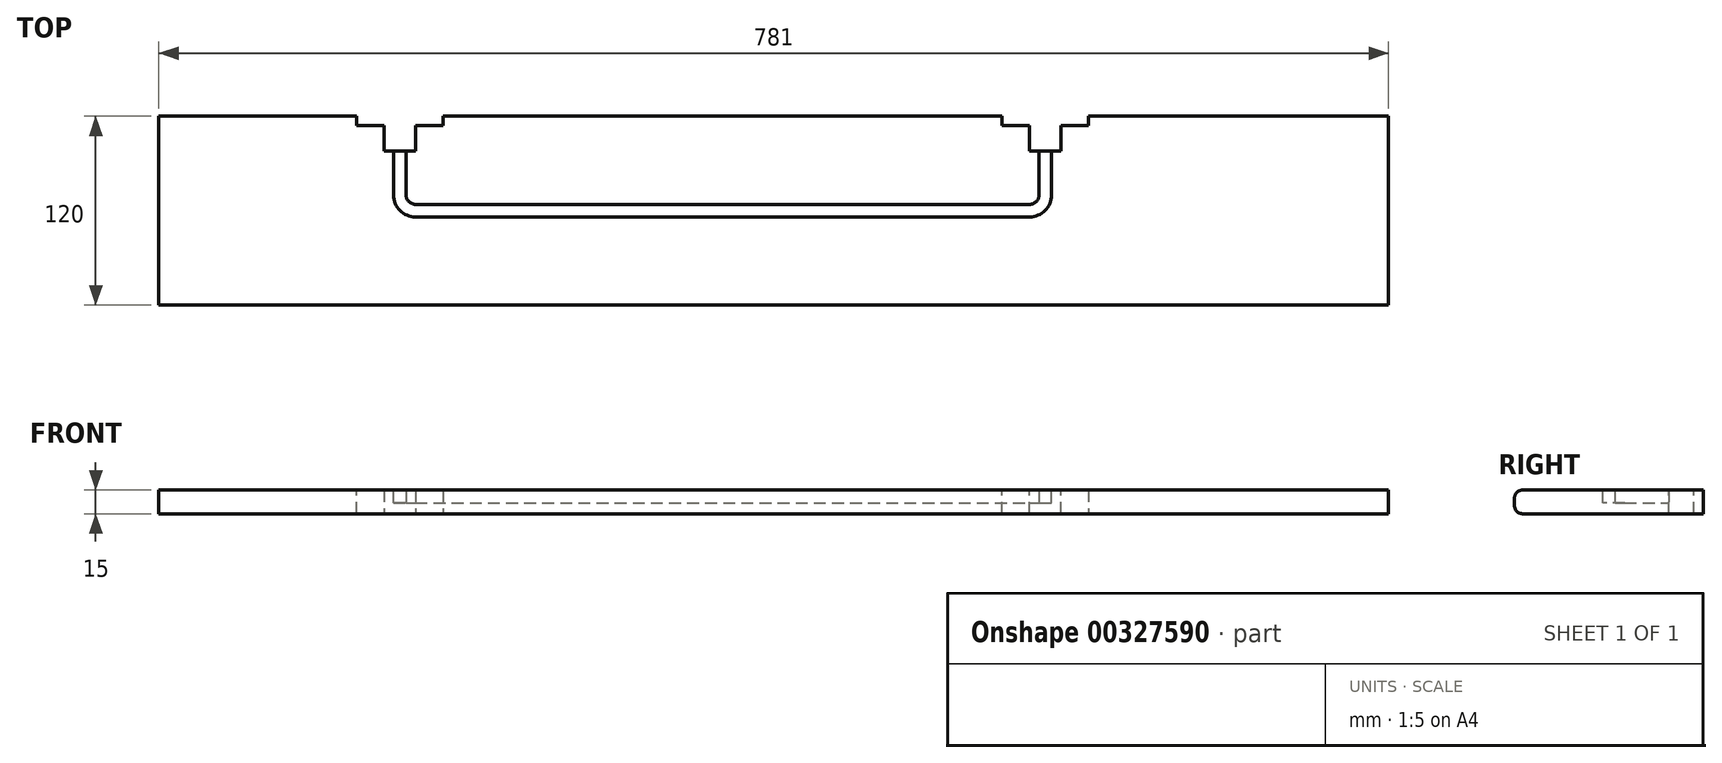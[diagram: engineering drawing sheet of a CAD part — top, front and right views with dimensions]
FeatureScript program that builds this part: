
annotation { "Feature Type Name" : "Feature", "Feature Type Description" : "" }
export const myFeature = defineFeature(function(context is Context, id is Id, definition is map)
    precondition{}
    {
        {
            var Q0;
            Q0=qCreatedBy(makeId("Right.planeOp"),FACE);
            var sketch = newSketch(context, id + "F0", { "sketchPlane" : qUnion([Q0])});
            skLineSegment(sketch, "E0.bottom", {"start": v(60, 7.5) * mm, "end": v(-60, 7.5) * mm});
            skLineSegment(sketch, "E0.top", {"start": v(60, -7.5) * mm, "end": v(-60, -7.5) * mm});
            skLineSegment(sketch, "E0.left", {"start": v(60, 7.5) * mm, "end": v(60, -7.5) * mm});
            skLineSegment(sketch, "E0.right", {"start": v(-60, 7.5) * mm, "end": v(-60, -7.5) * mm});
            skPoint(sketch, "E0.middle", {"position": v(0, 0) * mm});
            skSolve(sketch);
        }
        {
            var Q0;
            Q0=makeQuery(id+"F0.imprint","IMPRINT",FACE,{"disambiguationData":[TD([[makeQuery(id+"F0.imprint","IMPRINT",EDGE,{"derivedFrom":sQuery(id+"F0.wireOp",EDGE,"E0.bottom")}),1.0]])]});
            extrude(context, id + "F1", {"entities" : qUnion([Q0]), "depth" : 781 * mm});
        }
        {
            var Q0;
            Q0=makeQuery(id+"F1.opExtrude","SWEPT_FACE",FACE,{"disambiguationData":[OSD([sQuery(id+"F0.wireOp",EDGE,"E0.bottom")])]});
            var sketch = newSketch(context, id + "F2", { "sketchPlane" : qUnion([Q0])});
            skLineSegment(sketch, "E1", {"start": v(153, 60) * mm, "end": v(153, 10) * mm});
            skLineSegment(sketch, "E2", {"start": v(163, 0) * mm, "end": v(553, 0) * mm});
            skLineSegment(sketch, "E3", {"start": v(563, 0) * mm, "end": v(563, 0) * mm});
            skLineSegment(sketch, "E4", {"start": v(563, 10) * mm, "end": v(563, 60) * mm});
            skPoint(sketch, "E5.visualSharp", {"position": v(153, 0) * mm});
            skArc(sketch, "E5.filletArc", {"start": v(153, 10) * mm, "mid": v(155.93, 2.93) * mm, "end": v(163, 0) * mm});
            skPoint(sketch, "E6.visualSharp", {"position": v(563, 0) * mm});
            skArc(sketch, "E6.filletArc", {"start": v(553, 0) * mm, "mid": v(560.07, 2.93) * mm, "end": v(563, 10) * mm});
            skSolve(sketch);
        }
        {
            var Q0;
            Q0=makeQuery(id+"F1.opExtrude","SWEPT_FACE",FACE,{"disambiguationData":[OSD([sQuery(id+"F0.wireOp",EDGE,"E0.left")])]});
            var sketch = newSketch(context, id + "F3", { "sketchPlane" : qUnion([Q0])});
            skLineSegment(sketch, "E7.bottom", {"start": v(-148.99, -0.5) * mm, "end": v(-156.99, -0.5) * mm});
            skLineSegment(sketch, "E7.top", {"start": v(-148.99, 15.5) * mm, "end": v(-156.99, 15.5) * mm});
            skLineSegment(sketch, "E7.left", {"start": v(-148.99, -0.5) * mm, "end": v(-148.99, 15.5) * mm});
            skLineSegment(sketch, "E7.right", {"start": v(-156.99, -0.5) * mm, "end": v(-156.99, 15.5) * mm});
            skPoint(sketch, "E7.middle", {"position": v(-152.99, 7.5) * mm});
            skSolve(sketch);
        }
        {
            var Q0;
            {var subQ0=sQuery(id+"F3.wireOp",EDGE,"E7.top");Q0=makeQuery(id+"F3.imprint","IMPRINT",FACE,{"disambiguationData":[TD([[makeQuery(id+"F3.imprint","IMPRINT",EDGE,{"derivedFrom":subQ0}),1.0]])]});}
            var Q1;
            {var subQ0=sQuery(id+"F3.wireOp",EDGE,"E7.bottom");Q1=makeQuery(id+"F3.imprint","IMPRINT",FACE,{"disambiguationData":[TD([[makeQuery(id+"F3.imprint","IMPRINT",EDGE,{"derivedFrom":subQ0}),-1.0]])]});}
            var Q2;
            Q2=sQuery(id+"F2.wireOp",EDGE,"E1");
            var Q3;
            Q3=sQuery(id+"F2.wireOp",EDGE,"E5.filletArc");
            var Q4;
            Q4=sQuery(id+"F2.wireOp",EDGE,"E2");
            var Q5;
            Q5=sQuery(id+"F2.wireOp",EDGE,"E4");
            var Q6;
            Q6=sQuery(id+"F2.wireOp",EDGE,"E6.filletArc");
            sweep(context, id + "F4", {"operationType" : NewBodyOperationType.REMOVE, "profiles" : qUnion([Q0, Q1]), "path" : qUnion([Q2, Q3, Q4, Q5, Q6])});
        }
        {
            var Q0;
            {var subQ0=sQuery(id+"F0.wireOp",EDGE,"E0.right");var subQ4=sQuery(id+"F0.wireOp",EDGE,"E0.bottom");Q0=makeQuery(id+"F4.boolean.opBoolean","SPLIT",FACE,{"disambiguationData":[TD([makeQuery(id+"F1.opExtrude","SWEPT_FACE",FACE,{"disambiguationData":[OSD([subQ0])]})])],"derivedFrom":makeQuery(id+"F1.opExtrude","SWEPT_FACE",FACE,{"disambiguationData":[OSD([subQ4])]})});}
            var sketch = newSketch(context, id + "F5", { "sketchPlane" : qUnion([Q0])});
            skLineSegment(sketch, "E8.bottom", {"start": v(180.49, 54) * mm, "end": v(125.49, 54) * mm});
            skLineSegment(sketch, "E8.top", {"start": v(180.49, 66) * mm, "end": v(125.49, 66) * mm});
            skLineSegment(sketch, "E8.left", {"start": v(180.49, 54) * mm, "end": v(180.49, 66) * mm});
            skLineSegment(sketch, "E8.right", {"start": v(125.49, 54) * mm, "end": v(125.49, 66) * mm});
            skPoint(sketch, "E8.middle", {"position": v(152.99, 60) * mm});
            skLineSegment(sketch, "E9.bottom", {"start": v(535.51, 54) * mm, "end": v(590.51, 54) * mm});
            skLineSegment(sketch, "E9.top", {"start": v(535.51, 66) * mm, "end": v(590.51, 66) * mm});
            skLineSegment(sketch, "E9.left", {"start": v(535.51, 54) * mm, "end": v(535.51, 66) * mm});
            skLineSegment(sketch, "E9.right", {"start": v(590.51, 54) * mm, "end": v(590.51, 66) * mm});
            skPoint(sketch, "E9.middle", {"position": v(563.01, 60) * mm});
            skSolve(sketch);
        }
        {
            var Q0;
            {var subQ0=sQuery(id+"F5.wireOp",EDGE,"E8.right");var subQ1=sQuery(id+"F5.wireOp",EDGE,"E8.bottom");var subQ2=makeQuery(id+"F5.imprint","INTERSECT",VERTEX,{"derivedFrom":[subQ1,subQ0]});Q0=makeQuery(id+"F5.imprint","IMPRINT",FACE,{"disambiguationData":[TD([[makeQuery(id+"F5.imprint","IMPRINT",EDGE,{"disambiguationData":[TD([[subQ2,1.0]])],"derivedFrom":subQ1}),-1.0]])]});}
            var Q1;
            {var subQ1=sQuery(id+"F5.wireOp",EDGE,"E8.top");Q1=makeQuery(id+"F5.imprint","IMPRINT",FACE,{"disambiguationData":[TD([[makeQuery(id+"F5.imprint","IMPRINT",EDGE,{"derivedFrom":subQ1}),1.0]])]});}
            var Q2;
            {var subQ1=sQuery(id+"F5.wireOp",EDGE,"E9.top");Q2=makeQuery(id+"F5.imprint","IMPRINT",FACE,{"disambiguationData":[TD([[makeQuery(id+"F5.imprint","IMPRINT",EDGE,{"derivedFrom":subQ1}),-1.0]])]});}
            var Q3;
            {var subQ0=sQuery(id+"F5.wireOp",EDGE,"E9.right");var subQ1=sQuery(id+"F5.wireOp",EDGE,"E9.bottom");var subQ2=makeQuery(id+"F5.imprint","INTERSECT",VERTEX,{"derivedFrom":[subQ1,subQ0]});Q3=makeQuery(id+"F5.imprint","IMPRINT",FACE,{"disambiguationData":[TD([[makeQuery(id+"F5.imprint","IMPRINT",EDGE,{"disambiguationData":[TD([[subQ2,1.0]])],"derivedFrom":subQ1}),1.0]])]});}
            extrude(context, id + "F6", {"entities" : qUnion([Q0, Q1, Q2, Q3]), "operationType" : NewBodyOperationType.REMOVE, "oppositeDirection" : true, "depth" : 25 * mm});
        }
        {
            var Q0;
            {var subQ0=sQuery(id+"F0.wireOp",EDGE,"E0.right");var subQ4=sQuery(id+"F0.wireOp",EDGE,"E0.bottom");Q0=makeQuery(id+"F4.boolean.opBoolean","SPLIT",FACE,{"disambiguationData":[TD([makeQuery(id+"F1.opExtrude","SWEPT_FACE",FACE,{"disambiguationData":[OSD([subQ0])]})])],"derivedFrom":makeQuery(id+"F1.opExtrude","SWEPT_FACE",FACE,{"disambiguationData":[OSD([subQ4])]})});}
            var sketch = newSketch(context, id + "F7", { "sketchPlane" : qUnion([Q0])});
            skLineSegment(sketch, "E10.bottom", {"start": v(142.99, 38) * mm, "end": v(162.99, 38) * mm});
            skLineSegment(sketch, "E10.top", {"start": v(142.99, 70) * mm, "end": v(162.99, 70) * mm});
            skLineSegment(sketch, "E10.left", {"start": v(142.99, 38) * mm, "end": v(142.99, 70) * mm});
            skLineSegment(sketch, "E10.right", {"start": v(162.99, 38) * mm, "end": v(162.99, 70) * mm});
            skPoint(sketch, "E10.middle", {"position": v(152.99, 54) * mm});
            skPoint(sketch, "E10.middle.positionSnap0", {"position": v(137.24, 54) * mm});
            skPoint(sketch, "E10.centerSnap0", {"position": v(137.24, 54) * mm});
            skSolve(sketch);
        }
        {
            var Q0;
            {var subQ4=sQuery(id+"F0.wireOp",EDGE,"E0.bottom");Q0=makeQuery(id+"F7.imprint","IMPRINT",FACE,{"disambiguationData":[TD([[makeQuery(id+"F7.imprint","IMPRINT",EDGE,{"derivedFrom":makeQuery(id+"F1.opExtrude","CAP_EDGE",EDGE,{"disambiguationData":[OSD([subQ4])],"isStart":true})}),1.0]])]});}
            var sketch = newSketch(context, id + "F8", { "sketchPlane" : qUnion([Q0])});
            skLineSegment(sketch, "E11.bottom", {"start": v(573.01, 38) * mm, "end": v(553.01, 38) * mm});
            skLineSegment(sketch, "E11.top", {"start": v(573.01, 70) * mm, "end": v(553.01, 70) * mm});
            skLineSegment(sketch, "E11.left", {"start": v(573.01, 38) * mm, "end": v(573.01, 70) * mm});
            skLineSegment(sketch, "E11.right", {"start": v(553.01, 38) * mm, "end": v(553.01, 70) * mm});
            skPoint(sketch, "E11.middle", {"position": v(563.01, 54) * mm});
            skSolve(sketch);
        }
        {
            var Q0;
            {var subQ0=sQuery(id+"F7.wireOp",EDGE,"E10.left");var subQ1=sQuery(id+"F7.wireOp",EDGE,"E10.bottom");var subQ2=makeQuery(id+"F7.imprint","INTERSECT",VERTEX,{"derivedFrom":[subQ1,subQ0]});Q0=makeQuery(id+"F7.imprint","IMPRINT",FACE,{"disambiguationData":[TD([[makeQuery(id+"F7.imprint","IMPRINT",EDGE,{"disambiguationData":[TD([[subQ2,-1.0]])],"derivedFrom":subQ1}),1.0]])]});}
            var Q1;
            {var subQ2=sQuery(id+"F7.wireOp",EDGE,"E10.top");Q1=makeQuery(id+"F7.imprint","IMPRINT",FACE,{"disambiguationData":[TD([[makeQuery(id+"F7.imprint","IMPRINT",EDGE,{"derivedFrom":subQ2}),-1.0]])]});}
            extrude(context, id + "F9", {"entities" : qUnion([Q0, Q1]), "operationType" : NewBodyOperationType.REMOVE, "oppositeDirection" : true, "depth" : 25 * mm});
        }
        {
            var Q0;
            {var subQ0=sQuery(id+"F8.wireOp",EDGE,"E11.left");var subQ1=sQuery(id+"F8.wireOp",EDGE,"E11.bottom");var subQ2=makeQuery(id+"F8.imprint","INTERSECT",VERTEX,{"derivedFrom":[subQ1,subQ0]});Q0=makeQuery(id+"F8.imprint","IMPRINT",FACE,{"disambiguationData":[TD([[makeQuery(id+"F8.imprint","IMPRINT",EDGE,{"disambiguationData":[TD([[subQ2,-1.0]])],"derivedFrom":subQ1}),-1.0]])]});}
            var Q1;
            {var subQ2=sQuery(id+"F8.wireOp",EDGE,"E11.top");Q1=makeQuery(id+"F8.imprint","IMPRINT",FACE,{"disambiguationData":[TD([[makeQuery(id+"F8.imprint","IMPRINT",EDGE,{"derivedFrom":subQ2}),1.0]])]});}
            extrude(context, id + "F10", {"entities" : qUnion([Q0, Q1]), "operationType" : NewBodyOperationType.REMOVE, "oppositeDirection" : true, "depth" : 25 * mm});
        }
        {
            var Q0;
            Q0=makeQuery(id+"F1.opExtrude","SWEPT_EDGE",EDGE,{"disambiguationData":[OSD([sQuery(id+"F0.wireOp",EDGE,"E0.top"),sQuery(id+"F0.wireOp",EDGE,"E0.right")])]});
            var Q1;
            Q1=makeQuery(id+"F1.opExtrude","SWEPT_EDGE",EDGE,{"disambiguationData":[OSD([sQuery(id+"F0.wireOp",EDGE,"E0.bottom"),sQuery(id+"F0.wireOp",EDGE,"E0.right")])]});
            fillet(context, id + "F11", {"entities" : qUnion([Q0, Q1]), "radius" : 5 * mm, "tangentPropagation" : true, "allowEdgeOverflow" : false});
        }
    });
